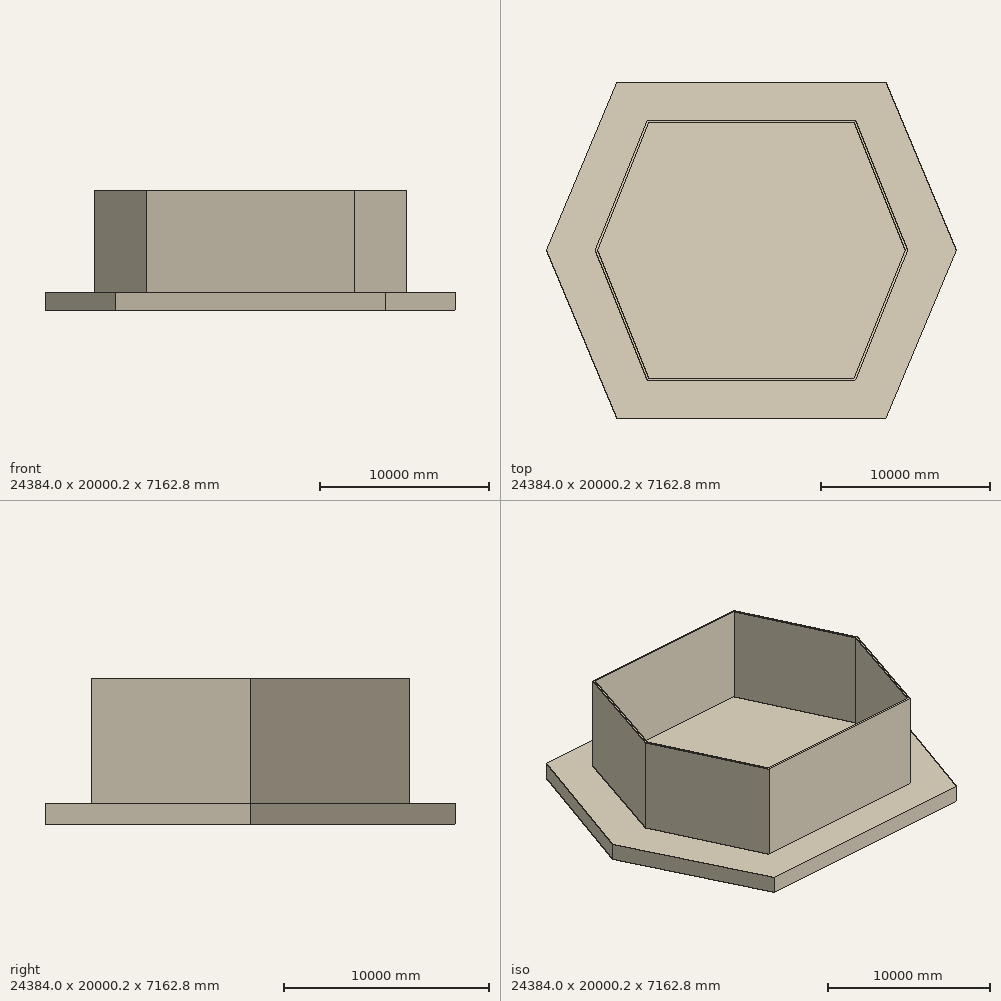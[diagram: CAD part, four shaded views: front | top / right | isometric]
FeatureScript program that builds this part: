
annotation { "Feature Type Name" : "Feature", "Feature Type Description" : "" }
export const myFeature = defineFeature(function(context is Context, id is Id, definition is map)
    precondition{}
    {
        {
            var Q0;
            Q0=qCreatedBy(makeId("Top.planeOp"),FACE);
            var sketch = newSketch(context, id + "F0", { "sketchPlane" : qUnion([Q0])});
            skLineSegment(sketch, "E0", {"start": v(0, 0) * mm, "end": v(9144, 0) * mm, "construction": true});
            skLineSegment(sketch, "E1", {"start": v(0, 0) * mm, "end": v(-9144, 0) * mm, "construction": true});
            skLineSegment(sketch, "E2", {"start": v(0, 0) * mm, "end": v(0, 7620) * mm, "construction": true});
            skLineSegment(sketch, "E3", {"start": v(0, 0) * mm, "end": v(0, -7620) * mm, "construction": true});
            skLineSegment(sketch, "E4", {"start": v(0, 7620) * mm, "end": v(-6096, 7620) * mm});
            skLineSegment(sketch, "E5", {"start": v(0, 7620) * mm, "end": v(6096, 7620) * mm});
            skLineSegment(sketch, "E6", {"start": v(6096, 7620) * mm, "end": v(9144, 0) * mm});
            skLineSegment(sketch, "E7", {"start": v(-6096, 7620) * mm, "end": v(-9144, 0) * mm});
            skLineSegment(sketch, "E8", {"start": v(0, -7620) * mm, "end": v(-6096, -7620) * mm});
            skLineSegment(sketch, "E9", {"start": v(0, -7620) * mm, "end": v(6096, -7620) * mm});
            skLineSegment(sketch, "E10", {"start": v(6096, -7620) * mm, "end": v(9144, 0) * mm});
            skLineSegment(sketch, "E11", {"start": v(-9144, 0) * mm, "end": v(-6096, -7620) * mm});
            skLineSegment(sketch, "E12", {"start": v(-6096, 7620) * mm, "end": v(6096, -7620) * mm, "construction": true});
            skLineSegment(sketch, "E13", {"start": v(6096, 7620) * mm, "end": v(-6096, -7620) * mm, "construction": true});
            skLineSegment(sketch, "E14", {"start": v(-6096, 7620) * mm, "end": v(-6191.2, 7739) * mm, "construction": true});
            skLineSegment(sketch, "E15", {"start": v(6096, 7620) * mm, "end": v(6191.2, 7739) * mm, "construction": true});
            skLineSegment(sketch, "E16", {"start": v(-6096, -7620) * mm, "end": v(-6191.2, -7739) * mm, "construction": true});
            skLineSegment(sketch, "E17", {"start": v(6096, -7620) * mm, "end": v(6191.2, -7739) * mm, "construction": true});
            skLineSegment(sketch, "E18", {"start": v(-9144, 0) * mm, "end": v(-9296.4, 0) * mm, "construction": true});
            skLineSegment(sketch, "E19", {"start": v(9144, 0) * mm, "end": v(9296.4, 0) * mm, "construction": true});
            skLineSegment(sketch, "E20", {"start": v(-6191.2, 7739) * mm, "end": v(-9296.4, 0) * mm});
            skLineSegment(sketch, "E21", {"start": v(-9296.4, 0) * mm, "end": v(-6191.2, -7739) * mm});
            skLineSegment(sketch, "E22", {"start": v(-6191.2, -7739) * mm, "end": v(6191.2, -7739) * mm});
            skLineSegment(sketch, "E23", {"start": v(9296.4, 0) * mm, "end": v(6191.2, 7739) * mm});
            skLineSegment(sketch, "E24", {"start": v(6191.2, 7739) * mm, "end": v(-6191.2, 7739) * mm});
            skLineSegment(sketch, "E25", {"start": v(9296.4, 0) * mm, "end": v(6191.2, -7739) * mm});
            skLineSegment(sketch, "E26", {"start": v(-6096, 7620) * mm, "end": v(-8000.07, 10000.09) * mm, "construction": true});
            skLineSegment(sketch, "E27", {"start": v(6096, 7620) * mm, "end": v(8000.07, 10000.09) * mm, "construction": true});
            skLineSegment(sketch, "E28", {"start": v(-6096, -7620) * mm, "end": v(-8000.07, -10000.09) * mm, "construction": true});
            skLineSegment(sketch, "E29", {"start": v(6096, -7620) * mm, "end": v(8000.07, -10000.09) * mm, "construction": true});
            skLineSegment(sketch, "E30", {"start": v(9144, 0) * mm, "end": v(12192, 0) * mm, "construction": true});
            skLineSegment(sketch, "E31", {"start": v(-9144, 0) * mm, "end": v(-12192, 0) * mm, "construction": true});
            skLineSegment(sketch, "E32", {"start": v(-8000.07, 10000.09) * mm, "end": v(-12192, 0) * mm});
            skLineSegment(sketch, "E33", {"start": v(-12192, 0) * mm, "end": v(-8000.07, -10000.09) * mm});
            skLineSegment(sketch, "E34", {"start": v(-8000.07, -10000.09) * mm, "end": v(8000.07, -10000.09) * mm});
            skLineSegment(sketch, "E35", {"start": v(8000.07, -10000.09) * mm, "end": v(12192, 0) * mm});
            skLineSegment(sketch, "E36", {"start": v(12192, 0) * mm, "end": v(8000.07, 10000.09) * mm});
            skLineSegment(sketch, "E37", {"start": v(8000.07, 10000.09) * mm, "end": v(-8000.07, 10000.09) * mm});
            skSolve(sketch);
        }
        {
            var Q0;
            Q0 = qSketchRegion(id + "F0", true);
            var Q1;
            Q1=makeQuery(id+"F0.imprint","IMPRINT",FACE,{"disambiguationData":[TD([[makeQuery(id+"F0.imprint","IMPRINT",EDGE,{"derivedFrom":sQuery(id+"F0.wireOp",EDGE,"E4")}),1.0]])]});
            extrude(context, id + "F1", {"entities" : qUnion([Q0, Q1]), "depth" : 1066.8 * mm, "offsetDistance" : 30.48 * mm});
        }
        {
            var Q0;
            Q0=makeQuery(id+"F0.imprint","IMPRINT",FACE,{"disambiguationData":[TD([[makeQuery(id+"F0.imprint","IMPRINT",EDGE,{"derivedFrom":sQuery(id+"F0.wireOp",EDGE,"E4")}),-1.0]])]});
            extrude(context, id + "F2", {"entities" : qUnion([Q0]), "depth" : 7162.8 * mm, "offsetDistance" : 30.48 * mm});
        }
    });
